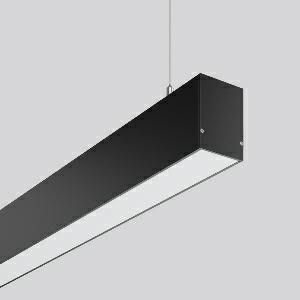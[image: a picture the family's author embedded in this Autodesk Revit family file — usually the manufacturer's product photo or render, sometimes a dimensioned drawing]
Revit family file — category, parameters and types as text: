
# Revit family: less_is_more_50_312318_003_e9ca
name_source: partatom
category: Lighting Fixtures
units: mm (PartAtom-declared; Revit-internal decimal feet)

## family parameters
Cut with Voids When Loaded = No
Host = Face
Light Source = No
Part Type = Normal
Room Calculation Point = No
Round Connector Dimension = Use Diameter
Shared = No

## types (1)
- LESS IS MORE 50 (1 x LED Modul 830, 4600 lm, 3000)
    Apparent Load = 40 VA
    CIE Flux Codes = 49 80 96 63 100
    Color Rendering = 80
    Color Temperature = 3000
    Default Elevation = 1800 mm
    Description = Series: LESS IS MORE 50
Linear pendant luminaire for aesthetically sophisticated lighting. Housing: extruded aluminium profile, powder-coated. End cap aluminium powder-coated. Canopy made of aluminium, powder-coated. Diffuser made of non-yellowing plastic (PMMA), opal. Direct 65%, indirect 35% light emission. Suitable for pendant. 2-point steel cable suspension freely positionable and infinitely height-adjustable. Special lengths available on request. LED unit with integrated converter interchangeable and removable. Suitable for through-wiring. With sensors or as a safety luminaire on request. 
Colour: deep black, matt (RAL 9005)
Length: 1127 mm
Width: 57 mm
Height: 75 mm
Suspension length: 2000 mm
Lamp: LED
Socket: without socket
Colour temperature: 3000K
Colour rendering index (CRI): 80
Light source: LED
Socket lamp2: Without base
Colour temperature: 3000K
System power: 40 W
Rated luminous flux: 4600 lm
Luminous efficiency: 115 lm/W
Control gear: Regulated power supply
Control gear: Regulated power supply
Protection class: I
Type of protection: IP 20
    Height = 75 mm
    Lamp = 1 x LED Modul 830
    Lamp Light Flux = 4600 lm
    Lamp count = 1
    Length = 1127 mm
    Lifetime = 50000 h
    Luminous efficacy = 115 lm/W
    Manufacturer = RZB
    ModVariant = No
    Model = 312318.003
    Mounting Place = Ceiling
    Mounting Type = Pendant
    Number of Poles = 1
    OnlyDefault = Yes
    Power Factor = 1
    Product Name = LESS IS MORE 50
    Product group = Pendant LED linear luminaires
    ProductGroupID = 907
    Protection Class = Protection class I
    Protection Degree = IP 20
    RLX_Detail_Level = 1
    RLX_Emergency_Light_Flux = 0 lm
    RLX_Emergency_Type = 0
    RLX_Emergency_Type_DB = No
    RlxData = <blob elided: 39869 chars, md5=b2023297>
    Socket = socket
    Standby Power = 0 W
    System Light Flux = 4600 lm
    System Power = 40 W
    Type Comments = Product without accessories
    Type Image = 312318.003.jpg
    URL = http://relux.com
    VarID = ---
    Voltage = 230 V
    Voltage Range = 220-240 V
    Weight = 0.00 kg
    Width = 57 mm

## geometry (parser evidence)
native form markers: Blend x4, Sweep x13
no freeform markers — native parametric forms only
